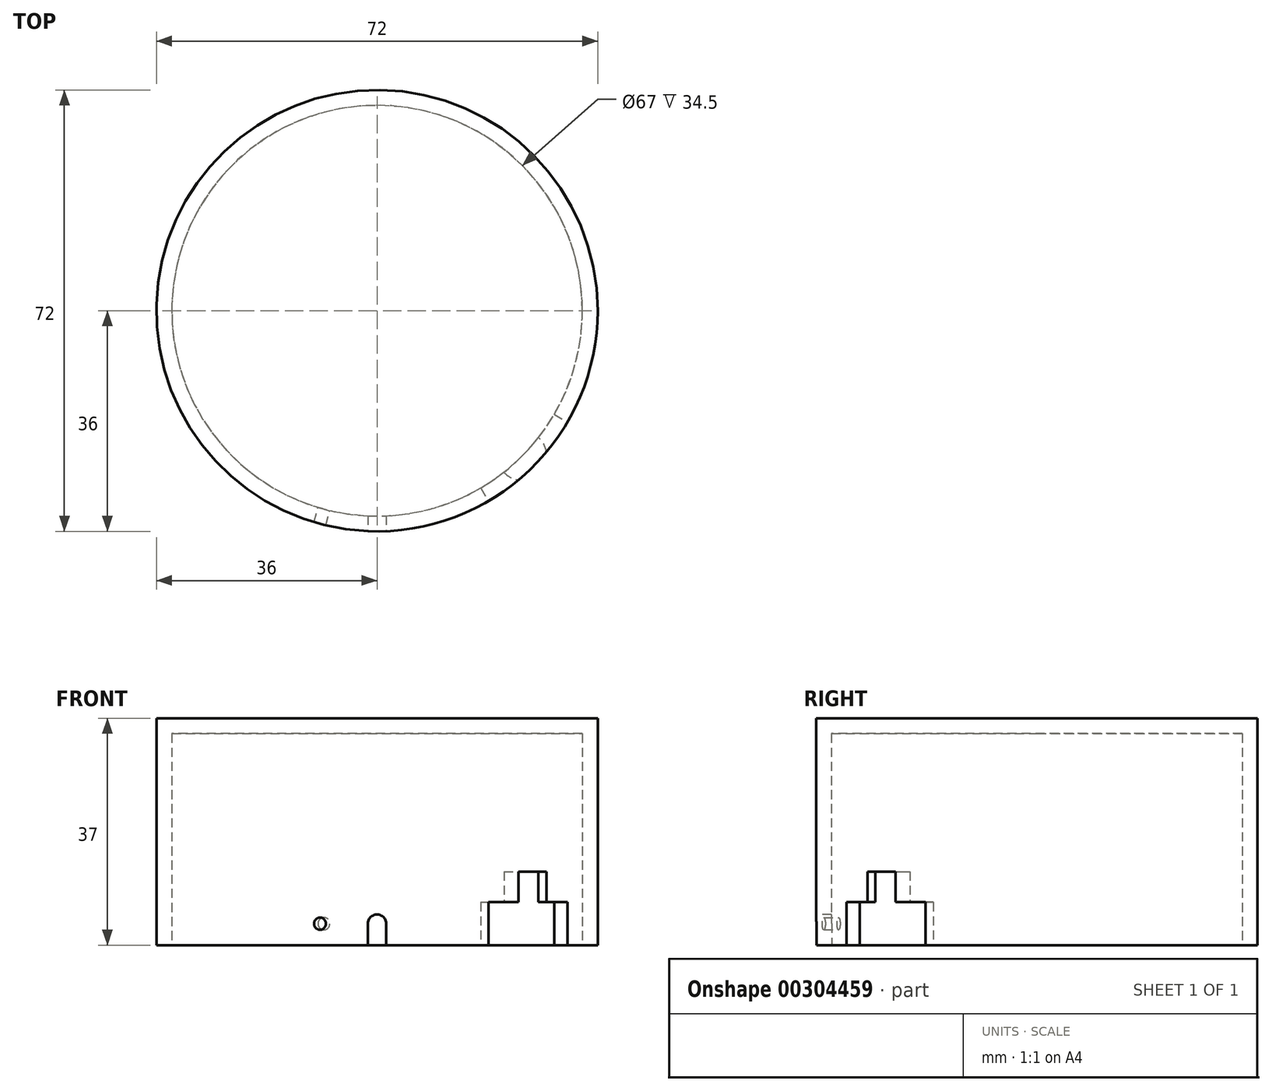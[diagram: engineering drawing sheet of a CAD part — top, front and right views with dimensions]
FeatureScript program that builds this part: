
annotation { "Feature Type Name" : "Feature", "Feature Type Description" : "" }
export const myFeature = defineFeature(function(context is Context, id is Id, definition is map)
    precondition{}
    {
        {
            var Q0;
            Q0=qCreatedBy(makeId("Top.planeOp"),FACE);
            var sketch = newSketch(context, id + "F0", { "sketchPlane" : qUnion([Q0])});
            skCircle(sketch, "E0", {"center": v(0, 0) * mm, "radius": 36 * mm});
            skSolve(sketch);
        }
        {
            var Q0;
            Q0 = qSketchRegion(id + "F0", true);
            extrude(context, id + "F1", {"entities" : qUnion([Q0]), "depth" : 37 * mm, "offsetDistance" : 25 * mm});
        }
        {
            var Q0;
            Q0=makeQuery(id+"F1.opExtrude","CAP_FACE",FACE,{"disambiguationData":[OSD([sQuery(id+"F0.wireOp",EDGE,"E0")])],"isStart":true});
            shell(context, id + "F2", {"entities" : qUnion([Q0]), "thickness" : 2.5 * mm});
        }
        {
            var Q0;
            Q0=qCreatedBy(makeId("Top.planeOp"),FACE);
            var sketch = newSketch(context, id + "F3", { "sketchPlane" : qUnion([Q0])});
            skCircle(sketch, "E1", {"center": v(0, 0) * mm, "radius": 36 * mm, "construction": true});
            skLineSegment(sketch, "E2", {"start": v(-30.16, 30.16) * mm, "end": v(31.04, -31.04) * mm, "construction": true});
            skLineSegment(sketch, "E3", {"start": v(-39.76, 0) * mm, "end": v(39.1, 0) * mm, "construction": true});
            skLineSegment(sketch, "E4", {"start": v(28.92, -16.9) * mm, "end": v(16.9, -28.92) * mm, "construction": true});
            skPoint(sketch, "E5", {"position": v(22.91, -22.91) * mm});
            skCircle(sketch, "E6", {"center": v(0, 0) * mm, "radius": 33.5 * mm, "construction": true});
            skLineSegment(sketch, "E7", {"start": v(0, 0) * mm, "end": v(32.53, -19) * mm, "construction": true});
            skLineSegment(sketch, "E8", {"start": v(0, 0) * mm, "end": v(18.66, -31.93) * mm, "construction": true});
            skArc(sketch, "E9", {"start": v(28.92, -16.9) * mm, "mid": v(23.69, -23.69) * mm, "end": v(16.9, -28.92) * mm});
            skArc(sketch, "E10", {"start": v(31.08, -18.16) * mm, "mid": v(25.46, -25.46) * mm, "end": v(18.16, -31.08) * mm});
            skLineSegment(sketch, "E11", {"start": v(28.92, -16.9) * mm, "end": v(31.08, -18.16) * mm});
            skLineSegment(sketch, "E12", {"start": v(16.9, -28.92) * mm, "end": v(18.16, -31.08) * mm});
            skSolve(sketch);
        }
        {
            var Q0;
            Q0 = qSketchRegion(id + "F3", true);
            extrude(context, id + "F4", {"entities" : qUnion([Q0]), "operationType" : NewBodyOperationType.REMOVE, "depth" : 7 * mm, "offsetDistance" : 25 * mm});
        }
        {
            var Q0;
            Q0=qCreatedBy(makeId("Top.planeOp"),FACE);
            var sketch = newSketch(context, id + "F5", { "sketchPlane" : qUnion([Q0])});
            skLineSegment(sketch, "E13", {"start": v(-43.18, 0) * mm, "end": v(44.93, 0) * mm, "construction": true});
            skLineSegment(sketch, "E14", {"start": v(-31.14, 31.14) * mm, "end": v(33.84, -33.84) * mm, "construction": true});
            skCircle(sketch, "E15", {"center": v(0, 0) * mm, "radius": 33.5 * mm, "construction": true});
            skCircle(sketch, "E16", {"center": v(23.69, -23.69) * mm, "radius": 4 * mm});
            skSolve(sketch);
        }
        {
            var Q0;
            Q0 = qSketchRegion(id + "F5", true);
            extrude(context, id + "F6", {"entities" : qUnion([Q0]), "operationType" : NewBodyOperationType.REMOVE, "depth" : 12 * mm, "offsetDistance" : 25 * mm});
        }
        {
            var Q0;
            Q0=qCreatedBy(makeId("Top.planeOp"),FACE);
            var sketch = newSketch(context, id + "F7", { "sketchPlane" : qUnion([Q0])});
            skLineSegment(sketch, "E17", {"start": v(-33.77, 0) * mm, "end": v(34, 0) * mm, "construction": true});
            skLineSegment(sketch, "E18", {"start": v(9.18, 34.25) * mm, "end": v(-9.34, -34.87) * mm, "construction": true});
            skSolve(sketch);
        }
        {
            var Q0;
            Q0=sQuery(id+"F7.wireOp",EDGE,"E18");
            var Q1;
            Q1=sQuery(id+"F7.wireOp",VERTEX,"E18.end");
            cPlane(context, id + "F8", {"entities" : qUnion([Q0, Q1]), "cplaneType" : CPlaneType.CURVE_POINT, "offset" : 25 * mm, "width" : 150 * mm, "height" : 150 * mm});
        }
        {
            var Q0;
            Q0=qCreatedBy(id+"F8.planeOp",FACE);
            var sketch = newSketch(context, id + "F9", { "sketchPlane" : qUnion([Q0])});
            skPoint(sketch, "E19", {"position": v(0, 3.5) * mm});
            skSolve(sketch);
        }
        {
            var Q0;
            Q0=sQuery(id+"F9.wireOp",VERTEX,"E19");
            var Q1;
            Q1=makeQuery(id+"F1.opExtrude","SWEPT_BODY",BODY,{"disambiguationData":[OSD([sQuery(id+"F0.wireOp",EDGE,"E0")])]});
            hole(context, id + "F10", {"style" : HoleStyle.SIMPLE, "endStyle" : HoleEndStyle.BLIND, "holeDiameter" : 2 * mm, "holeDepth" : 10 * mm, "tappedDepth" : 12 * mm, "tapClearance" : 3, "locations" : qUnion([Q0]), "scope" : qUnion([Q1]), "startStyle" : HoleStartStyle.SKETCH});
        }
        {
            var Q0;
            Q0=qCreatedBy(makeId("Top.planeOp"),FACE);
            var sketch = newSketch(context, id + "F11", { "sketchPlane" : qUnion([Q0])});
            skLineSegment(sketch, "E20", {"start": v(0, 37.14) * mm, "end": v(0, -36) * mm, "construction": true});
            skSolve(sketch);
        }
        {
            var Q0;
            Q0=sQuery(id+"F11.wireOp",EDGE,"E20");
            var Q1;
            Q1=sQuery(id+"F11.wireOp",VERTEX,"E20.end");
            cPlane(context, id + "F12", {"entities" : qUnion([Q0, Q1]), "cplaneType" : CPlaneType.CURVE_POINT, "offset" : 25 * mm, "width" : 150 * mm, "height" : 150 * mm});
        }
        {
            var Q0;
            Q0=qCreatedBy(id+"F12.planeOp",FACE);
            var sketch = newSketch(context, id + "F13", { "sketchPlane" : qUnion([Q0])});
            skCircle(sketch, "E21", {"center": v(0, 3.5) * mm, "radius": 1.5 * mm, "construction": true});
            skArc(sketch, "E22", {"start": v(-1.5, 3.5) * mm, "mid": v(0, 5) * mm, "end": v(1.5, 3.5) * mm});
            skLineSegment(sketch, "E23", {"start": v(-1.5, 3.5) * mm, "end": v(-1.5, 0) * mm});
            skLineSegment(sketch, "E24", {"start": v(-1.5, 0) * mm, "end": v(1.5, 0) * mm});
            skLineSegment(sketch, "E25", {"start": v(1.5, 0) * mm, "end": v(1.5, 3.5) * mm});
            skSolve(sketch);
        }
        {
            var Q0;
            Q0 = qSketchRegion(id + "F13", true);
            extrude(context, id + "F14", {"entities" : qUnion([Q0]), "operationType" : NewBodyOperationType.REMOVE, "oppositeDirection" : true, "depth" : 5 * mm, "offsetDistance" : 25 * mm});
        }
    });
